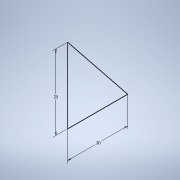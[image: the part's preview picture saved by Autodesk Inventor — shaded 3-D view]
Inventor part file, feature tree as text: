
AUTODESK INVENTOR PART (.ipt)
format: ipt  version: 2020.2 (Build 242310000, 310)  size: 94,720 bytes
history: native  units: mm
features: extrude x1, sketch x1
ambient origin geometry x8: Origin, YZ Plane, XZ Plane, XY Plane, X Axis, Y Axis, Z Axis, Center Point
bodies: Solido1 (feature_tree)
feature tree (2):
  extrude  "Estrusione1"  Depth=16.0mm
  sketch  "Schizzo1"
